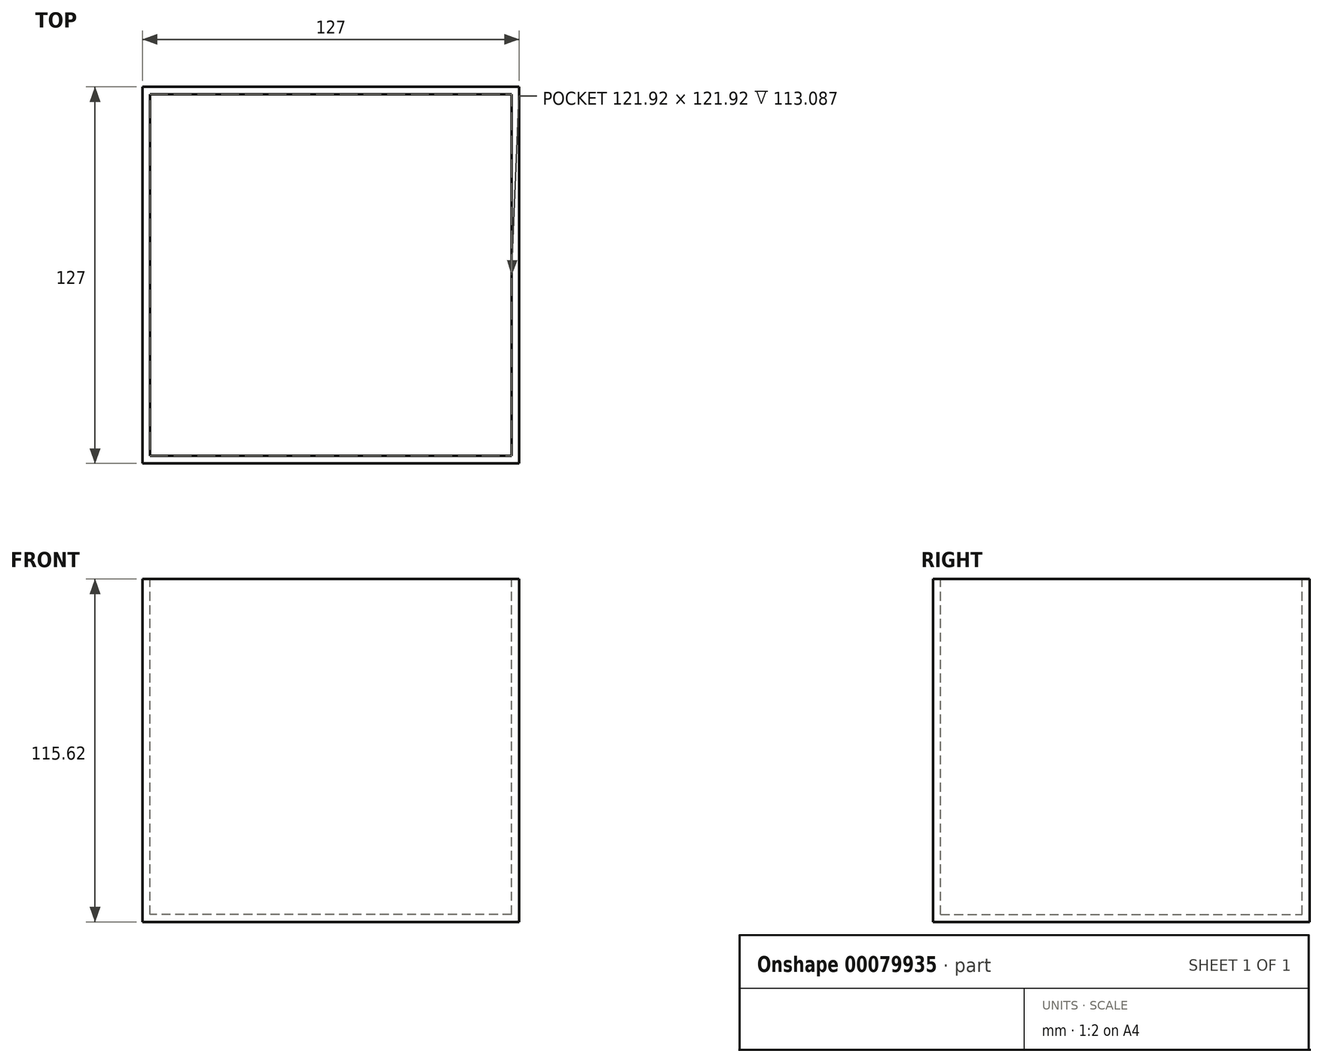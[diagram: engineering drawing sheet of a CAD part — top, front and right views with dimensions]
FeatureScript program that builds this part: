
annotation { "Feature Type Name" : "Feature", "Feature Type Description" : "" }
export const myFeature = defineFeature(function(context is Context, id is Id, definition is map)
    precondition{}
    {
        {
            var Q0;
            Q0=qCreatedBy(makeId("Front.planeOp"),FACE);
            var sketch = newSketch(context, id + "F0", { "sketchPlane" : qUnion([Q0])});
            skLineSegment(sketch, "E0.bottom", {"start": v(63.5, -57.81) * mm, "end": v(-63.5, -57.81) * mm});
            skLineSegment(sketch, "E0.top", {"start": v(63.5, 57.81) * mm, "end": v(-63.5, 57.81) * mm});
            skLineSegment(sketch, "E0.left", {"start": v(63.5, -57.81) * mm, "end": v(63.5, 57.81) * mm});
            skLineSegment(sketch, "E0.right", {"start": v(-63.5, -57.81) * mm, "end": v(-63.5, 57.81) * mm});
            skPoint(sketch, "E0.middle", {"position": v(0, 0) * mm});
            skSolve(sketch);
        }
        {
            var Q0;
            Q0=makeQuery(id+"F0.imprint","IMPRINT",FACE,{"disambiguationData":[TD([[makeQuery(id+"F0.imprint","IMPRINT",EDGE,{"derivedFrom":sQuery(id+"F0.wireOp",EDGE,"E0.bottom")}),-1.0]])]});
            extrude(context, id + "F1", {"entities" : qUnion([Q0]), "depth" : 127 * mm});
        }
        {
            var Q0;
            Q0=makeQuery(id+"F1.opExtrude","SWEPT_FACE",FACE,{"disambiguationData":[OSD([sQuery(id+"F0.wireOp",EDGE,"E0.top")])]});
            shell(context, id + "F2", {"entities" : qUnion([Q0]), "thickness" : 2.54 * mm});
        }
    });
